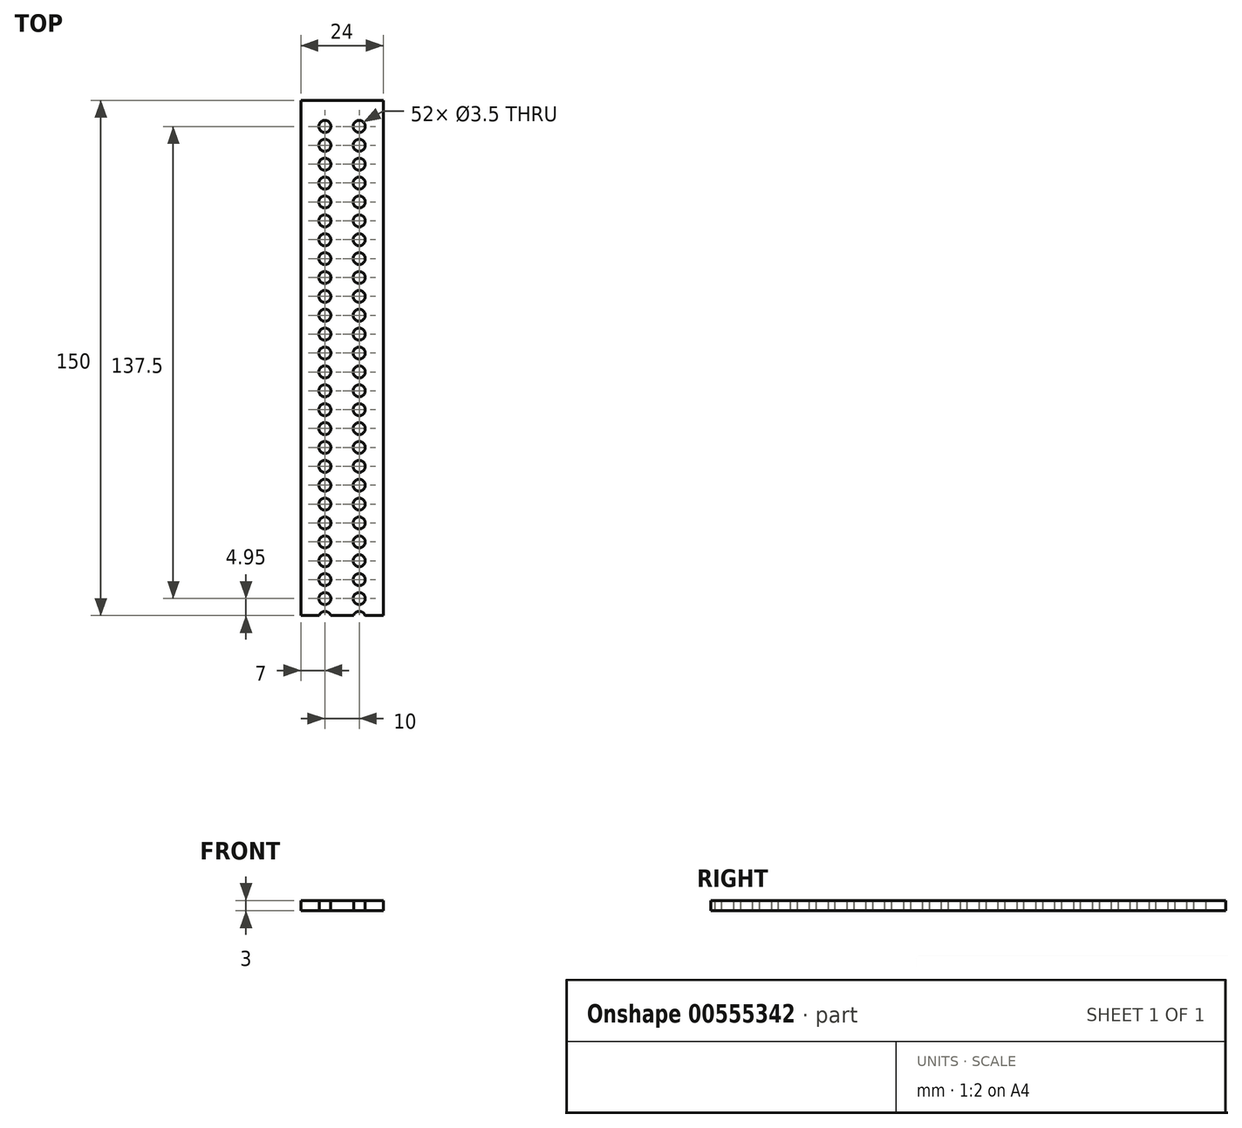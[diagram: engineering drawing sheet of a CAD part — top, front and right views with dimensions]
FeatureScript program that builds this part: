
annotation { "Feature Type Name" : "Feature", "Feature Type Description" : "" }
export const myFeature = defineFeature(function(context is Context, id is Id, definition is map)
    precondition{}
    {
        {
            var Q0;
            Q0=qCreatedBy(makeId("Front.planeOp"),FACE);
            var sketch = newSketch(context, id + "F0", { "sketchPlane" : qUnion([Q0])});
            skLineSegment(sketch, "E0.bottom", {"start": v(0, 0) * mm, "end": v(24, 0) * mm});
            skLineSegment(sketch, "E0.top", {"start": v(0, -3) * mm, "end": v(24, -3) * mm});
            skLineSegment(sketch, "E0.left", {"start": v(0, 0) * mm, "end": v(0, -3) * mm});
            skLineSegment(sketch, "E0.right", {"start": v(24, 0) * mm, "end": v(24, -3) * mm});
            skSolve(sketch);
        }
        {
            var Q0;
            Q0 = qSketchRegion(id + "F0", true);
            extrude(context, id + "F1", {"entities" : qUnion([Q0]), "depth" : 150 * mm, "offsetDistance" : 25 * mm});
        }
        {
            var Q0;
            Q0=makeQuery(id+"F1.opExtrude","SWEPT_FACE",FACE,{"disambiguationData":[OSD([sQuery(id+"F0.wireOp",EDGE,"E0.bottom")])]});
            var sketch = newSketch(context, id + "F2", { "sketchPlane" : qUnion([Q0])});
            skCircle(sketch, "E1", {"center": v(7, -7.55) * mm, "radius": 1.75 * mm});
            skPoint(sketch, "E1.centerSnap0", {"position": v(7, 0) * mm});
            skCircle(sketch, "E2", {"center": v(17, -7.55) * mm, "radius": 1.75 * mm});
            skPoint(sketch, "E2.centerSnap0", {"position": v(17, 0) * mm});
            skCircle(sketch, "E3.1.0.0", {"center": v(17, -13.05) * mm, "radius": 1.75 * mm});
            skCircle(sketch, "E3.1.0.1", {"center": v(7, -13.05) * mm, "radius": 1.75 * mm});
            skCircle(sketch, "E3.2.0.0", {"center": v(17, -18.55) * mm, "radius": 1.75 * mm});
            skCircle(sketch, "E3.2.0.1", {"center": v(7, -18.55) * mm, "radius": 1.75 * mm});
            skCircle(sketch, "E3.3.0.0", {"center": v(17, -24.05) * mm, "radius": 1.75 * mm});
            skCircle(sketch, "E3.3.0.1", {"center": v(7, -24.05) * mm, "radius": 1.75 * mm});
            skCircle(sketch, "E3.4.0.0", {"center": v(17, -29.55) * mm, "radius": 1.75 * mm});
            skCircle(sketch, "E3.4.0.1", {"center": v(7, -29.55) * mm, "radius": 1.75 * mm});
            skCircle(sketch, "E3.5.0.0", {"center": v(17, -35.05) * mm, "radius": 1.75 * mm});
            skCircle(sketch, "E3.5.0.1", {"center": v(7, -35.05) * mm, "radius": 1.75 * mm});
            skCircle(sketch, "E3.6.0.0", {"center": v(17, -40.55) * mm, "radius": 1.75 * mm});
            skCircle(sketch, "E3.6.0.1", {"center": v(7, -40.55) * mm, "radius": 1.75 * mm});
            skCircle(sketch, "E3.7.0.0", {"center": v(17, -46.05) * mm, "radius": 1.75 * mm});
            skCircle(sketch, "E3.7.0.1", {"center": v(7, -46.05) * mm, "radius": 1.75 * mm});
            skCircle(sketch, "E3.8.0.0", {"center": v(17, -51.55) * mm, "radius": 1.75 * mm});
            skCircle(sketch, "E3.8.0.1", {"center": v(7, -51.55) * mm, "radius": 1.75 * mm});
            skCircle(sketch, "E3.9.0.0", {"center": v(17, -57.05) * mm, "radius": 1.75 * mm});
            skCircle(sketch, "E3.9.0.1", {"center": v(7, -57.05) * mm, "radius": 1.75 * mm});
            skCircle(sketch, "E3.10.0.0", {"center": v(17, -62.55) * mm, "radius": 1.75 * mm});
            skCircle(sketch, "E3.10.0.1", {"center": v(7, -62.55) * mm, "radius": 1.75 * mm});
            skCircle(sketch, "E3.11.0.0", {"center": v(17, -68.05) * mm, "radius": 1.75 * mm});
            skCircle(sketch, "E3.11.0.1", {"center": v(7, -68.05) * mm, "radius": 1.75 * mm});
            skCircle(sketch, "E3.12.0.0", {"center": v(17, -73.55) * mm, "radius": 1.75 * mm});
            skCircle(sketch, "E3.12.0.1", {"center": v(7, -73.55) * mm, "radius": 1.75 * mm});
            skCircle(sketch, "E3.13.0.0", {"center": v(17, -79.05) * mm, "radius": 1.75 * mm});
            skCircle(sketch, "E3.13.0.1", {"center": v(7, -79.05) * mm, "radius": 1.75 * mm});
            skCircle(sketch, "E3.14.0.0", {"center": v(17, -84.55) * mm, "radius": 1.75 * mm});
            skCircle(sketch, "E3.14.0.1", {"center": v(7, -84.55) * mm, "radius": 1.75 * mm});
            skCircle(sketch, "E3.15.0.0", {"center": v(17, -90.05) * mm, "radius": 1.75 * mm});
            skCircle(sketch, "E3.15.0.1", {"center": v(7, -90.05) * mm, "radius": 1.75 * mm});
            skCircle(sketch, "E3.16.0.0", {"center": v(17, -95.55) * mm, "radius": 1.75 * mm});
            skCircle(sketch, "E3.16.0.1", {"center": v(7, -95.55) * mm, "radius": 1.75 * mm});
            skCircle(sketch, "E3.17.0.0", {"center": v(17, -101.05) * mm, "radius": 1.75 * mm});
            skCircle(sketch, "E3.17.0.1", {"center": v(7, -101.05) * mm, "radius": 1.75 * mm});
            skCircle(sketch, "E3.18.0.0", {"center": v(17, -106.55) * mm, "radius": 1.75 * mm});
            skCircle(sketch, "E3.18.0.1", {"center": v(7, -106.55) * mm, "radius": 1.75 * mm});
            skCircle(sketch, "E3.19.0.0", {"center": v(17, -112.05) * mm, "radius": 1.75 * mm});
            skCircle(sketch, "E3.19.0.1", {"center": v(7, -112.05) * mm, "radius": 1.75 * mm});
            skCircle(sketch, "E3.20.0.0", {"center": v(17, -117.55) * mm, "radius": 1.75 * mm});
            skCircle(sketch, "E3.20.0.1", {"center": v(7, -117.55) * mm, "radius": 1.75 * mm});
            skCircle(sketch, "E3.21.0.0", {"center": v(17, -123.05) * mm, "radius": 1.75 * mm});
            skCircle(sketch, "E3.21.0.1", {"center": v(7, -123.05) * mm, "radius": 1.75 * mm});
            skCircle(sketch, "E3.22.0.0", {"center": v(17, -128.55) * mm, "radius": 1.75 * mm});
            skCircle(sketch, "E3.22.0.1", {"center": v(7, -128.55) * mm, "radius": 1.75 * mm});
            skCircle(sketch, "E3.23.0.0", {"center": v(17, -134.05) * mm, "radius": 1.75 * mm});
            skCircle(sketch, "E3.23.0.1", {"center": v(7, -134.05) * mm, "radius": 1.75 * mm});
            skCircle(sketch, "E3.24.0.0", {"center": v(17, -139.55) * mm, "radius": 1.75 * mm});
            skCircle(sketch, "E3.24.0.1", {"center": v(7, -139.55) * mm, "radius": 1.75 * mm});
            skCircle(sketch, "E3.25.0.0", {"center": v(17, -145.05) * mm, "radius": 1.75 * mm});
            skCircle(sketch, "E3.25.0.1", {"center": v(7, -145.05) * mm, "radius": 1.75 * mm});
            skCircle(sketch, "E3.26.0.0", {"center": v(17, -150.55) * mm, "radius": 1.75 * mm});
            skCircle(sketch, "E3.26.0.1", {"center": v(7, -150.55) * mm, "radius": 1.75 * mm});
            skCircle(sketch, "E3.27.0.0", {"center": v(17, -156.05) * mm, "radius": 1.75 * mm});
            skCircle(sketch, "E3.27.0.1", {"center": v(7, -156.05) * mm, "radius": 1.75 * mm});
            skLineSegment(sketch, "E3.direction1", {"start": v(17, -7.55) * mm, "end": v(17, -13.05) * mm, "construction": true});
            skSolve(sketch);
        }
        {
            var Q0;
            Q0=makeQuery(id+"F2.imprint","IMPRINT",FACE,{"disambiguationData":[TD([[makeQuery(id+"F2.imprint","IMPRINT",EDGE,{"derivedFrom":sQuery(id+"F2.wireOp",EDGE,"E1")}),1.0]])]});
            var Q1;
            Q1=makeQuery(id+"F2.imprint","IMPRINT",FACE,{"disambiguationData":[TD([[makeQuery(id+"F2.imprint","IMPRINT",EDGE,{"derivedFrom":sQuery(id+"F2.wireOp",EDGE,"E2")}),1.0]])]});
            var Q2;
            Q2=makeQuery(id+"F2.imprint","IMPRINT",FACE,{"disambiguationData":[TD([[makeQuery(id+"F2.imprint","IMPRINT",EDGE,{"derivedFrom":sQuery(id+"F2.wireOp",EDGE,"E3.6.0.1")}),1.0]])]});
            var Q3;
            Q3=makeQuery(id+"F2.imprint","IMPRINT",FACE,{"disambiguationData":[TD([[makeQuery(id+"F2.imprint","IMPRINT",EDGE,{"derivedFrom":sQuery(id+"F2.wireOp",EDGE,"E3.7.0.1")}),1.0]])]});
            var Q4;
            Q4=makeQuery(id+"F2.imprint","IMPRINT",FACE,{"disambiguationData":[TD([[makeQuery(id+"F2.imprint","IMPRINT",EDGE,{"derivedFrom":sQuery(id+"F2.wireOp",EDGE,"E3.14.0.0")}),1.0]])]});
            var Q5;
            Q5=makeQuery(id+"F2.imprint","IMPRINT",FACE,{"disambiguationData":[TD([[makeQuery(id+"F2.imprint","IMPRINT",EDGE,{"derivedFrom":sQuery(id+"F2.wireOp",EDGE,"E3.9.0.0")}),1.0]])]});
            var Q6;
            Q6=makeQuery(id+"F2.imprint","IMPRINT",FACE,{"disambiguationData":[TD([[makeQuery(id+"F2.imprint","IMPRINT",EDGE,{"derivedFrom":sQuery(id+"F2.wireOp",EDGE,"E3.12.0.0")}),1.0]])]});
            var Q7;
            Q7=makeQuery(id+"F2.imprint","IMPRINT",FACE,{"disambiguationData":[TD([[makeQuery(id+"F2.imprint","IMPRINT",EDGE,{"derivedFrom":sQuery(id+"F2.wireOp",EDGE,"E3.5.0.0")}),1.0]])]});
            var Q8;
            Q8=makeQuery(id+"F2.imprint","IMPRINT",FACE,{"disambiguationData":[TD([[makeQuery(id+"F2.imprint","IMPRINT",EDGE,{"derivedFrom":sQuery(id+"F2.wireOp",EDGE,"E3.4.0.0")}),1.0]])]});
            var Q9;
            Q9=makeQuery(id+"F2.imprint","IMPRINT",FACE,{"disambiguationData":[TD([[makeQuery(id+"F2.imprint","IMPRINT",EDGE,{"derivedFrom":sQuery(id+"F2.wireOp",EDGE,"E3.3.0.0")}),1.0]])]});
            var Q10;
            Q10=makeQuery(id+"F2.imprint","IMPRINT",FACE,{"disambiguationData":[TD([[makeQuery(id+"F2.imprint","IMPRINT",EDGE,{"derivedFrom":sQuery(id+"F2.wireOp",EDGE,"E3.2.0.0")}),1.0]])]});
            var Q11;
            Q11=makeQuery(id+"F2.imprint","IMPRINT",FACE,{"disambiguationData":[TD([[makeQuery(id+"F2.imprint","IMPRINT",EDGE,{"derivedFrom":sQuery(id+"F2.wireOp",EDGE,"E3.6.0.0")}),1.0]])]});
            var Q12;
            Q12=makeQuery(id+"F2.imprint","IMPRINT",FACE,{"disambiguationData":[TD([[makeQuery(id+"F2.imprint","IMPRINT",EDGE,{"derivedFrom":sQuery(id+"F2.wireOp",EDGE,"E3.7.0.0")}),1.0]])]});
            var Q13;
            Q13=makeQuery(id+"F2.imprint","IMPRINT",FACE,{"disambiguationData":[TD([[makeQuery(id+"F2.imprint","IMPRINT",EDGE,{"derivedFrom":sQuery(id+"F2.wireOp",EDGE,"E3.16.0.0")}),1.0]])]});
            var Q14;
            Q14=makeQuery(id+"F2.imprint","IMPRINT",FACE,{"disambiguationData":[TD([[makeQuery(id+"F2.imprint","IMPRINT",EDGE,{"derivedFrom":sQuery(id+"F2.wireOp",EDGE,"E3.8.0.0")}),1.0]])]});
            var Q15;
            Q15=makeQuery(id+"F2.imprint","IMPRINT",FACE,{"disambiguationData":[TD([[makeQuery(id+"F2.imprint","IMPRINT",EDGE,{"derivedFrom":sQuery(id+"F2.wireOp",EDGE,"E3.11.0.0")}),1.0]])]});
            var Q16;
            Q16=makeQuery(id+"F2.imprint","IMPRINT",FACE,{"disambiguationData":[TD([[makeQuery(id+"F2.imprint","IMPRINT",EDGE,{"derivedFrom":sQuery(id+"F2.wireOp",EDGE,"E3.10.0.0")}),1.0]])]});
            var Q17;
            Q17=makeQuery(id+"F2.imprint","IMPRINT",FACE,{"disambiguationData":[TD([[makeQuery(id+"F2.imprint","IMPRINT",EDGE,{"derivedFrom":sQuery(id+"F2.wireOp",EDGE,"E3.13.0.0")}),1.0]])]});
            var Q18;
            Q18=makeQuery(id+"F2.imprint","IMPRINT",FACE,{"disambiguationData":[TD([[makeQuery(id+"F2.imprint","IMPRINT",EDGE,{"derivedFrom":sQuery(id+"F2.wireOp",EDGE,"E3.17.0.1")}),1.0]])]});
            var Q19;
            Q19=makeQuery(id+"F2.imprint","IMPRINT",FACE,{"disambiguationData":[TD([[makeQuery(id+"F2.imprint","IMPRINT",EDGE,{"derivedFrom":sQuery(id+"F2.wireOp",EDGE,"E3.9.0.1")}),1.0]])]});
            var Q20;
            Q20=makeQuery(id+"F2.imprint","IMPRINT",FACE,{"disambiguationData":[TD([[makeQuery(id+"F2.imprint","IMPRINT",EDGE,{"derivedFrom":sQuery(id+"F2.wireOp",EDGE,"E3.12.0.1")}),1.0]])]});
            var Q21;
            Q21=makeQuery(id+"F2.imprint","IMPRINT",FACE,{"disambiguationData":[TD([[makeQuery(id+"F2.imprint","IMPRINT",EDGE,{"derivedFrom":sQuery(id+"F2.wireOp",EDGE,"E3.20.0.1")}),1.0]])]});
            var Q22;
            Q22=makeQuery(id+"F2.imprint","IMPRINT",FACE,{"disambiguationData":[TD([[makeQuery(id+"F2.imprint","IMPRINT",EDGE,{"derivedFrom":sQuery(id+"F2.wireOp",EDGE,"E3.16.0.1")}),1.0]])]});
            var Q23;
            Q23=makeQuery(id+"F2.imprint","IMPRINT",FACE,{"disambiguationData":[TD([[makeQuery(id+"F2.imprint","IMPRINT",EDGE,{"derivedFrom":sQuery(id+"F2.wireOp",EDGE,"E3.11.0.1")}),1.0]])]});
            var Q24;
            Q24=makeQuery(id+"F2.imprint","IMPRINT",FACE,{"disambiguationData":[TD([[makeQuery(id+"F2.imprint","IMPRINT",EDGE,{"derivedFrom":sQuery(id+"F2.wireOp",EDGE,"E3.19.0.1")}),1.0]])]});
            var Q25;
            Q25=makeQuery(id+"F2.imprint","IMPRINT",FACE,{"disambiguationData":[TD([[makeQuery(id+"F2.imprint","IMPRINT",EDGE,{"derivedFrom":sQuery(id+"F2.wireOp",EDGE,"E3.18.0.1")}),1.0]])]});
            var Q26;
            Q26=makeQuery(id+"F2.imprint","IMPRINT",FACE,{"disambiguationData":[TD([[makeQuery(id+"F2.imprint","IMPRINT",EDGE,{"derivedFrom":sQuery(id+"F2.wireOp",EDGE,"E3.10.0.1")}),1.0]])]});
            var Q27;
            Q27=makeQuery(id+"F2.imprint","IMPRINT",FACE,{"disambiguationData":[TD([[makeQuery(id+"F2.imprint","IMPRINT",EDGE,{"derivedFrom":sQuery(id+"F2.wireOp",EDGE,"E3.15.0.1")}),1.0]])]});
            var Q28;
            Q28=makeQuery(id+"F2.imprint","IMPRINT",FACE,{"disambiguationData":[TD([[makeQuery(id+"F2.imprint","IMPRINT",EDGE,{"derivedFrom":sQuery(id+"F2.wireOp",EDGE,"E3.13.0.1")}),1.0]])]});
            var Q29;
            Q29=makeQuery(id+"F2.imprint","IMPRINT",FACE,{"disambiguationData":[TD([[makeQuery(id+"F2.imprint","IMPRINT",EDGE,{"derivedFrom":sQuery(id+"F2.wireOp",EDGE,"E3.14.0.1")}),1.0]])]});
            var Q30;
            Q30=makeQuery(id+"F2.imprint","IMPRINT",FACE,{"disambiguationData":[TD([[makeQuery(id+"F2.imprint","IMPRINT",EDGE,{"derivedFrom":sQuery(id+"F2.wireOp",EDGE,"E3.22.0.0")}),1.0]])]});
            var Q31;
            Q31=makeQuery(id+"F2.imprint","IMPRINT",FACE,{"disambiguationData":[TD([[makeQuery(id+"F2.imprint","IMPRINT",EDGE,{"derivedFrom":sQuery(id+"F2.wireOp",EDGE,"E3.25.0.0")}),1.0]])]});
            var Q32;
            Q32=makeQuery(id+"F2.imprint","IMPRINT",FACE,{"disambiguationData":[TD([[makeQuery(id+"F2.imprint","IMPRINT",EDGE,{"derivedFrom":sQuery(id+"F2.wireOp",EDGE,"E3.17.0.0")}),1.0]])]});
            var Q33;
            Q33=makeQuery(id+"F2.imprint","IMPRINT",FACE,{"disambiguationData":[TD([[makeQuery(id+"F2.imprint","IMPRINT",EDGE,{"derivedFrom":sQuery(id+"F2.wireOp",EDGE,"E3.20.0.0")}),1.0]])]});
            var Q34;
            Q34=makeQuery(id+"F2.imprint","IMPRINT",FACE,{"disambiguationData":[TD([[makeQuery(id+"F2.imprint","IMPRINT",EDGE,{"derivedFrom":sQuery(id+"F2.wireOp",EDGE,"E3.23.0.0")}),1.0]])]});
            var Q35;
            Q35=makeQuery(id+"F2.imprint","IMPRINT",FACE,{"disambiguationData":[TD([[makeQuery(id+"F2.imprint","IMPRINT",EDGE,{"derivedFrom":sQuery(id+"F2.wireOp",EDGE,"E3.24.0.0")}),1.0]])]});
            var Q36;
            Q36=makeQuery(id+"F2.imprint","IMPRINT",FACE,{"disambiguationData":[TD([[makeQuery(id+"F2.imprint","IMPRINT",EDGE,{"derivedFrom":sQuery(id+"F2.wireOp",EDGE,"E3.19.0.0")}),1.0]])]});
            var Q37;
            Q37=makeQuery(id+"F2.imprint","IMPRINT",FACE,{"disambiguationData":[TD([[makeQuery(id+"F2.imprint","IMPRINT",EDGE,{"derivedFrom":sQuery(id+"F2.wireOp",EDGE,"E3.27.0.0")}),1.0]])]});
            var Q38;
            Q38=makeQuery(id+"F2.imprint","IMPRINT",FACE,{"disambiguationData":[TD([[makeQuery(id+"F2.imprint","IMPRINT",EDGE,{"derivedFrom":sQuery(id+"F2.wireOp",EDGE,"E3.26.0.0")}),1.0]])]});
            var Q39;
            Q39=makeQuery(id+"F2.imprint","IMPRINT",FACE,{"disambiguationData":[TD([[makeQuery(id+"F2.imprint","IMPRINT",EDGE,{"derivedFrom":sQuery(id+"F2.wireOp",EDGE,"E3.18.0.0")}),1.0]])]});
            var Q40;
            Q40=makeQuery(id+"F2.imprint","IMPRINT",FACE,{"disambiguationData":[TD([[makeQuery(id+"F2.imprint","IMPRINT",EDGE,{"derivedFrom":sQuery(id+"F2.wireOp",EDGE,"E3.21.0.0")}),1.0]])]});
            var Q41;
            Q41=makeQuery(id+"F2.imprint","IMPRINT",FACE,{"disambiguationData":[TD([[makeQuery(id+"F2.imprint","IMPRINT",EDGE,{"derivedFrom":sQuery(id+"F2.wireOp",EDGE,"E3.25.0.1")}),1.0]])]});
            var Q42;
            Q42=makeQuery(id+"F2.imprint","IMPRINT",FACE,{"disambiguationData":[TD([[makeQuery(id+"F2.imprint","IMPRINT",EDGE,{"derivedFrom":sQuery(id+"F2.wireOp",EDGE,"E3.24.0.1")}),1.0]])]});
            var Q43;
            Q43=makeQuery(id+"F2.imprint","IMPRINT",FACE,{"disambiguationData":[TD([[makeQuery(id+"F2.imprint","IMPRINT",EDGE,{"derivedFrom":sQuery(id+"F2.wireOp",EDGE,"E3.27.0.1")}),1.0]])]});
            var Q44;
            Q44=makeQuery(id+"F2.imprint","IMPRINT",FACE,{"disambiguationData":[TD([[makeQuery(id+"F2.imprint","IMPRINT",EDGE,{"derivedFrom":sQuery(id+"F2.wireOp",EDGE,"E3.23.0.1")}),1.0]])]});
            var Q45;
            Q45=makeQuery(id+"F2.imprint","IMPRINT",FACE,{"disambiguationData":[TD([[makeQuery(id+"F2.imprint","IMPRINT",EDGE,{"derivedFrom":sQuery(id+"F2.wireOp",EDGE,"E3.26.0.1")}),1.0]])]});
            var Q46;
            Q46=makeQuery(id+"F2.imprint","IMPRINT",FACE,{"disambiguationData":[TD([[makeQuery(id+"F2.imprint","IMPRINT",EDGE,{"derivedFrom":sQuery(id+"F2.wireOp",EDGE,"E3.22.0.1")}),1.0]])]});
            var Q47;
            Q47=makeQuery(id+"F2.imprint","IMPRINT",FACE,{"disambiguationData":[TD([[makeQuery(id+"F2.imprint","IMPRINT",EDGE,{"derivedFrom":sQuery(id+"F2.wireOp",EDGE,"E3.21.0.1")}),1.0]])]});
            var Q48;
            Q48=makeQuery(id+"F2.imprint","IMPRINT",FACE,{"disambiguationData":[TD([[makeQuery(id+"F2.imprint","IMPRINT",EDGE,{"derivedFrom":sQuery(id+"F2.wireOp",EDGE,"E3.15.0.0")}),1.0]])]});
            var Q49;
            Q49=makeQuery(id+"F2.imprint","IMPRINT",FACE,{"disambiguationData":[TD([[makeQuery(id+"F2.imprint","IMPRINT",EDGE,{"derivedFrom":sQuery(id+"F2.wireOp",EDGE,"E3.8.0.1")}),1.0]])]});
            var Q50;
            Q50=makeQuery(id+"F2.imprint","IMPRINT",FACE,{"disambiguationData":[TD([[makeQuery(id+"F2.imprint","IMPRINT",EDGE,{"derivedFrom":sQuery(id+"F2.wireOp",EDGE,"E3.1.0.0")}),1.0]])]});
            var Q51;
            Q51=makeQuery(id+"F2.imprint","IMPRINT",FACE,{"disambiguationData":[TD([[makeQuery(id+"F2.imprint","IMPRINT",EDGE,{"derivedFrom":sQuery(id+"F2.wireOp",EDGE,"E3.5.0.1")}),1.0]])]});
            var Q52;
            Q52=makeQuery(id+"F2.imprint","IMPRINT",FACE,{"disambiguationData":[TD([[makeQuery(id+"F2.imprint","IMPRINT",EDGE,{"derivedFrom":sQuery(id+"F2.wireOp",EDGE,"E3.4.0.1")}),1.0]])]});
            var Q53;
            Q53=makeQuery(id+"F2.imprint","IMPRINT",FACE,{"disambiguationData":[TD([[makeQuery(id+"F2.imprint","IMPRINT",EDGE,{"derivedFrom":sQuery(id+"F2.wireOp",EDGE,"E3.3.0.1")}),1.0]])]});
            var Q54;
            Q54=makeQuery(id+"F2.imprint","IMPRINT",FACE,{"disambiguationData":[TD([[makeQuery(id+"F2.imprint","IMPRINT",EDGE,{"derivedFrom":sQuery(id+"F2.wireOp",EDGE,"E3.2.0.1")}),1.0]])]});
            var Q55;
            Q55=makeQuery(id+"F2.imprint","IMPRINT",FACE,{"disambiguationData":[TD([[makeQuery(id+"F2.imprint","IMPRINT",EDGE,{"derivedFrom":sQuery(id+"F2.wireOp",EDGE,"E3.1.0.1")}),1.0]])]});
            extrude(context, id + "F3", {"entities" : qUnion([Q0, Q1, Q2, Q3, Q4, Q5, Q6, Q7, Q8, Q9, Q10, Q11, Q12, Q13, Q14, Q15, Q16, Q17, Q18, Q19, Q20, Q21, Q22, Q23, Q24, Q25, Q26, Q27, Q28, Q29, Q30, Q31, Q32, Q33, Q34, Q35, Q36, Q37, Q38, Q39, Q40, Q41, Q42, Q43, Q44, Q45, Q46, Q47, Q48, Q49, Q50, Q51, Q52, Q53, Q54, Q55]), "operationType" : NewBodyOperationType.REMOVE, "oppositeDirection" : true, "depth" : 25 * mm, "offsetDistance" : 25 * mm});
        }
    });
